# Revit family: 18508-presto
name_source: partatom
category: Plumbing Fixtures
units: mm (PartAtom-declared; Revit-internal decimal feet)

## family parameters
Always vertical = Yes
Cut with Voids When Loaded = No
Maintain Annotation Orientation = No
OmniClass Number = 23.45.00.00
OmniClass Title = Sanitary, Laundry, and Cleaning Equipment
Part Type = Normal
Room Calculation Point = No
Round Connector Dimension = Use Diameter
Shared = No
Work Plane-Based = Yes

## types (1)
- 18508-presto
    Default Elevation = 1219 mm
    Description = Cas 1 : traversée d’une paroi verticale non résistante au feu en ERP
Cas 2 : traversée d’une paroi verticale résistante au feu en ERP, sous conditions de mise en œuvre indiquées dans la notice et les schémas d’intégration détaillés.
Cette configuration est valable pour épaisseur de la cloison maximum 56mm (équivalent 2 BA13 + carrelage par exemple). Pour autres types de cloison, il appartient à l'installateur ou le gestionnaire d'adapter l’évacuation (pipe d’évacuation et manchon) à son installation et aux exigences de compatibilité avec les cloisons coupe-feu, suivant le procès-verbal de résistance au feu de la paroi concernée et le règlement de sécurité mentionné ci dessus.
Accès par l’arrière obligatoire pour la maintenance.
    Manufacturer = presto
    Model = 18508
    RANGE = ELF-SUPPORTING MOUNTING FRAME WITH DIRECT FLUSH VALVE
    Recommended pressure = 3 bar
    URL = https://www.prestodatashare.com
    flow = 9.0 L/s
    flow time = 1.0 s
    min pressure = 1 bar

## geometry (parser evidence)
native form markers: Sweep x3
no freeform markers — native parametric forms only
